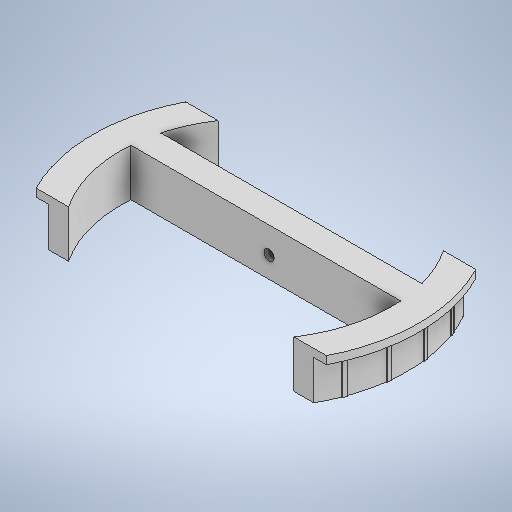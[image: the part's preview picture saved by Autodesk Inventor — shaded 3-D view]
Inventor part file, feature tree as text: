
AUTODESK INVENTOR PART (.ipt)
format: ipt  version: 2025 (Build 290162010, 162A)  size: 399,872 bytes
history: native  units: in
note: dims shown in document units (in); Inventor stores cm internally (conversion verified against a paired STEP export)
features: sketch x4, extrude x2, hole x1
ambient origin geometry x8: Origin, YZ Plane, XZ Plane, XY Plane, X Axis, Y Axis, Z Axis, Center Point
bodies: Solid1 (feature_tree)
feature tree (7):
  extrude  "Extrusion1"  Depth=0.0984in
  extrude  "Extrusion2"  Depth=0.0394in
  hole  "Hole1"  [1 undecoded]
  sketch  "Sketch1"  dims[d0=3.0433in d1=0.1679in d2=0.0984in]
  sketch  "Sketch Circular Pattern2"  dims[d3=0.1378in d10=0.0394in]
  sketch  "Sketch2"  dims[d11=0.0157in d12=10.2362in d14=360.0deg]
  sketch  "Sketch3"  dims[d16=0.5118in d17=0.8465in d18=1.5217in d19=0.1967in d20=0.3937in d21=0.0in d22=3.2677in d23=0.1181in d24=1.6339in d25=0.2559in d26=0.0787in d27=0.0in d28=0.26in d29=1.3827in d30=0.104in d31=0.17in d32=0.1575in d33=0.0787in d34=90.0deg d35=0.4322in d36=0.0in]
note: 1 required parameter value undecoded (feature->parameter linkage not recoverable at this tier; creation-order binding heuristic only, values carry confidence <= 0.55)
